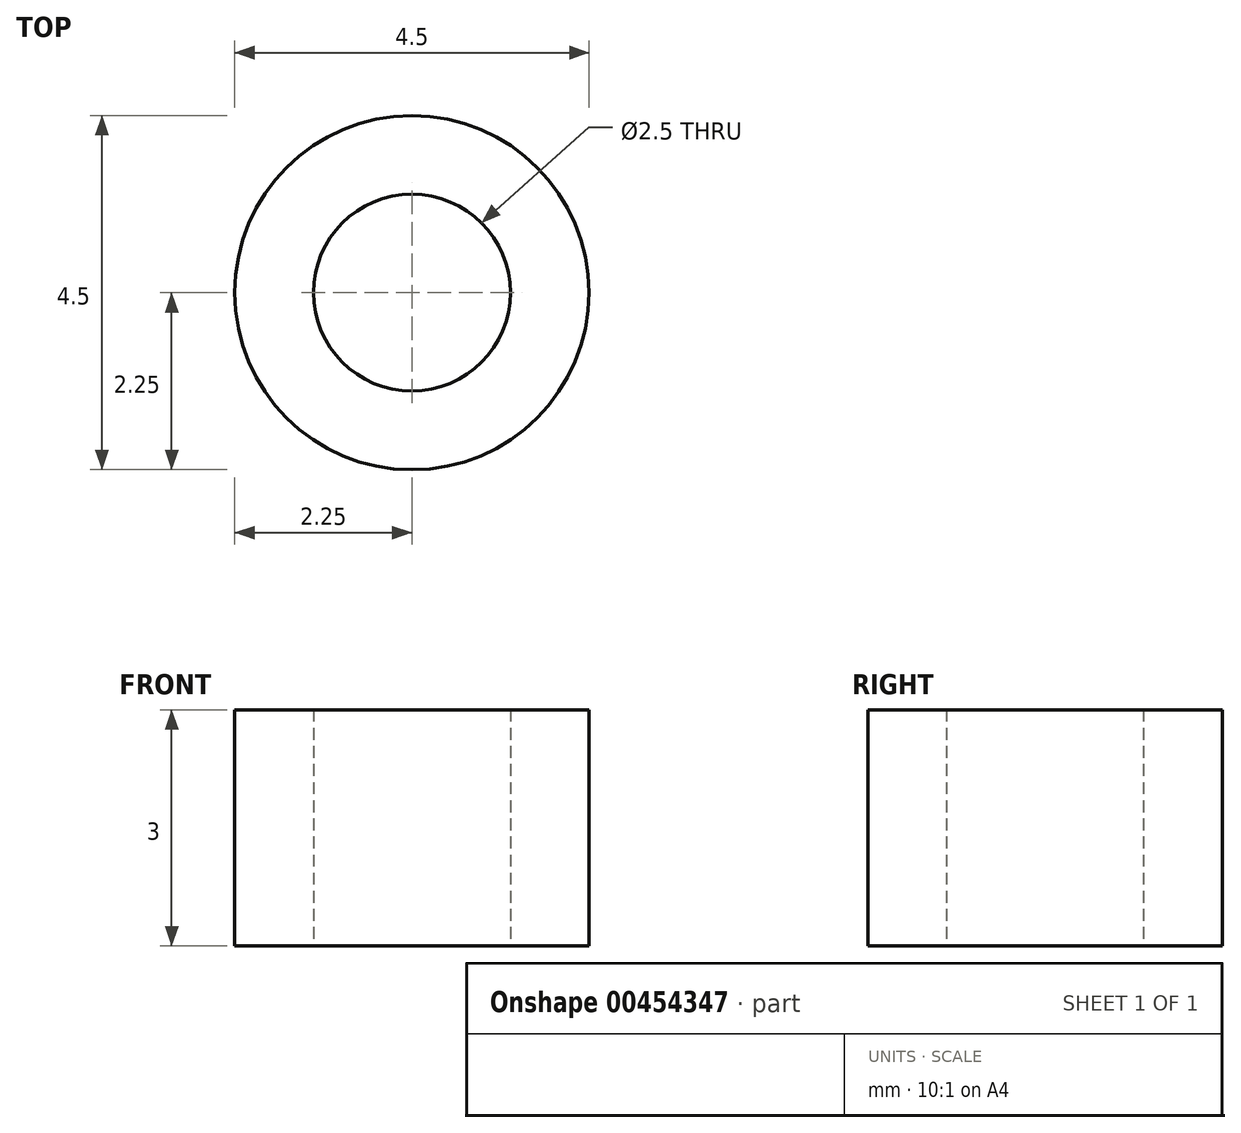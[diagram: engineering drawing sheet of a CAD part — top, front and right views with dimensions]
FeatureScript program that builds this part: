
annotation { "Feature Type Name" : "Feature", "Feature Type Description" : "" }
export const myFeature = defineFeature(function(context is Context, id is Id, definition is map)
    precondition{}
    {
        {
            var Q0;
            Q0=qCreatedBy(makeId("Top.planeOp"),FACE);
            var sketch = newSketch(context, id + "F0", { "sketchPlane" : qUnion([Q0])});
            skCircle(sketch, "E0", {"center": v(0, 0) * mm, "radius": 2.25 * mm});
            skCircle(sketch, "E1", {"center": v(0, 0) * mm, "radius": 1.25 * mm});
            skSolve(sketch);
        }
        {
            var Q0;
            Q0=makeQuery(id+"F0.imprint","IMPRINT",FACE,{"disambiguationData":[TD([[makeQuery(id+"F0.imprint","IMPRINT",EDGE,{"derivedFrom":sQuery(id+"F0.wireOp",EDGE,"E0")}),1.0]])]});
            extrude(context, id + "F1", {"entities" : qUnion([Q0]), "depth" : 3 * mm});
        }
    });
